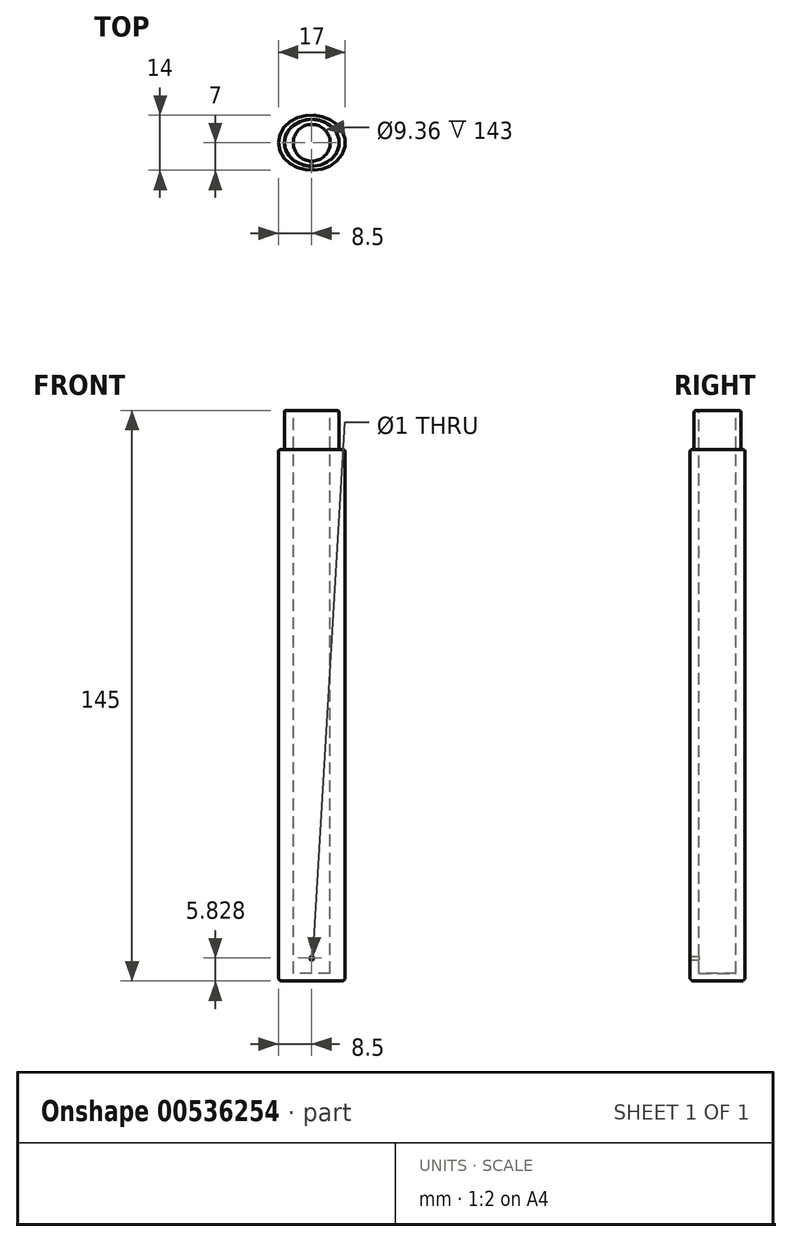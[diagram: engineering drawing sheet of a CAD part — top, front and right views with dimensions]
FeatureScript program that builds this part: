
annotation { "Feature Type Name" : "Feature", "Feature Type Description" : "" }
export const myFeature = defineFeature(function(context is Context, id is Id, definition is map)
    precondition{}
    {
        {
            var Q0;
            Q0=qCreatedBy(makeId("Top.planeOp"),FACE);
            var sketch = newSketch(context, id + "F0", { "sketchPlane" : qUnion([Q0])});
            skEllipse(sketch, "E0", {"center": v(0, 0) * mm, "majorRadius": 8.5 * mm, "minorRadius": 7 * mm, "majorAxis": v(-1, 0)});
            skCircle(sketch, "E1", {"center": v(0, 0) * mm, "radius": 4.55 * mm});
            skSolve(sketch);
        }
        {
            var Q0;
            Q0=qSketchRegion(id+"F0",true);
            var Q1;
            Q1=makeQuery(id+"F0.imprint","IMPRINT",FACE,{"disambiguationData":[TD([[makeQuery(id+"F0.imprint","IMPRINT",EDGE,{"derivedFrom":sQuery(id+"F0.wireOp",EDGE,"E1")}),1.0]])]});
            extrude(context, id + "F1", {"entities" : qUnion([Q0, Q1]), "depth" : 135 * mm});
        }
        {
            var Q0;
            Q0=makeQuery(id+"F1.opExtrude","CAP_FACE",FACE,{"disambiguationData":[OSD([sQuery(id+"F0.wireOp",EDGE,"E0")])],"isStart":false});
            var sketch = newSketch(context, id + "F2", { "sketchPlane" : qUnion([Q0])});
            skEllipse(sketch, "E2", {"center": v(0, 0) * mm, "majorRadius": 6.95 * mm, "minorRadius": 5.95 * mm, "majorAxis": v(-1, 0)});
            skSolve(sketch);
        }
        {
            var Q0;
            Q0=makeQuery(id+"F2.imprint","IMPRINT",FACE,{"disambiguationData":[TD([[makeQuery(id+"F2.imprint","IMPRINT",EDGE,{"derivedFrom":sQuery(id+"F2.wireOp",EDGE,"E2")}),1.0]])]});
            extrude(context, id + "F3", {"entities" : qUnion([Q0]), "operationType" : NewBodyOperationType.ADD, "depth" : 10 * mm});
        }
        {
            var Q0;
            Q0=makeQuery(id+"F3.opExtrude","CAP_FACE",FACE,{"disambiguationData":[OSD([sQuery(id+"F2.wireOp",EDGE,"E2")])],"isStart":false});
            var sketch = newSketch(context, id + "F4", { "sketchPlane" : qUnion([Q0])});
            skCircle(sketch, "E3", {"center": v(0, 0) * mm, "radius": 4.68 * mm});
            skSolve(sketch);
        }
        {
            var Q0;
            Q0=makeQuery(id+"F4.imprint","IMPRINT",FACE,{"disambiguationData":[TD([[makeQuery(id+"F4.imprint","IMPRINT",EDGE,{"derivedFrom":sQuery(id+"F4.wireOp",EDGE,"E3")}),1.0]])]});
            extrude(context, id + "F5", {"entities" : qUnion([Q0]), "operationType" : NewBodyOperationType.REMOVE, "oppositeDirection" : true, "depth" : 143 * mm});
        }
        {
            var Q0;
            Q0=makeQuery(id+"F5.boolean.opBoolean","COPY",EDGE,{"derivedFrom":makeQuery(id+"F5.opExtrude","CAP_EDGE",EDGE,{"disambiguationData":[OSD([sQuery(id+"F4.wireOp",EDGE,"E3")])],"isStart":true})});
            var Q1;
            Q1=makeQuery(id+"F3.opExtrude","CAP_EDGE",EDGE,{"disambiguationData":[OSD([sQuery(id+"F2.wireOp",EDGE,"E2")])],"isStart":false});
            var Q2;
            Q2=makeQuery(id+"F1.opExtrude","CAP_EDGE",EDGE,{"disambiguationData":[OSD([sQuery(id+"F0.wireOp",EDGE,"E0")])],"isStart":false});
            fillet(context, id + "F6", {"entities" : qUnion([Q0, Q1, Q2]), "radius" : .5 * mm, "tangentPropagation" : true, "allowEdgeOverflow" : false});
        }
        {
            var Q0;
            Q0=makeQuery(id+"F1.opExtrude","CAP_EDGE",EDGE,{"disambiguationData":[OSD([sQuery(id+"F0.wireOp",EDGE,"E0")])],"isStart":true});
            fillet(context, id + "F7", {"entities" : qUnion([Q0]), "radius" : 1 * mm, "tangentPropagation" : true, "allowEdgeOverflow" : false});
        }
        {
            var Q0;
            Q0=qCreatedBy(makeId("Front.planeOp"),FACE);
            var sketch = newSketch(context, id + "F8", { "sketchPlane" : qUnion([Q0])});
            skCircle(sketch, "E4", {"center": v(0, 5.83) * mm, "radius": 0.5 * mm});
            skSolve(sketch);
        }
        {
            var Q0;
            Q0=qSketchRegion(id+"F8",true);
            extrude(context, id + "F9", {"entities" : qUnion([Q0]), "operationType" : NewBodyOperationType.REMOVE, "depth" : 25 * mm});
        }
    });
